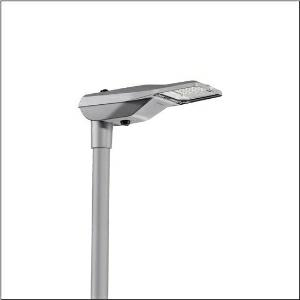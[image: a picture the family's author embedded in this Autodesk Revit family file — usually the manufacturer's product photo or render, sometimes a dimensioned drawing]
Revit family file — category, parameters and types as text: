
# Revit family: streetlight_sl_21_iq_micro___st0_8a_5xe1c31y08db_8273
name_source: partatom
category: Lighting Fixtures
units: mm (PartAtom-declared; Revit-internal decimal feet)

## family parameters
Cut with Voids When Loaded = No
Host = Face
Light Source = No
Part Type = Normal
Room Calculation Point = No
Round Connector Dimension = Use Diameter
Shared = No

## types (1)
- --- (1 x LED, 5110 lm, 39.1 W, 3000K)
    Apparent Load = 39 VA
    CIE Flux Codes = 38 75 97 100 100
    Color Rendering = 70
    Color Temperature = 3000K
    Default Elevation = 1800 mm
    Description = Streetlight SL 21 iQ micro, mast luminaire, primary light control with lens, of PMMA, primary optical cover: cover, of toughened safety glass, transparent, light distribution: ST0.8a, light emission: direct distribution, primary light characteristic: asymmetric, installation type: post-top, side-entry, LED, High Power LED, rated luminous flux: 5.110lm, luminous efficacy: 131lm/W, light colour: 730, colour temperature: 3000K, control gear: iQ-Street Remote, D4i with power reduction, control: pre-setting: logarithmic dimming characteristic, Street-Remote, Auto-Match, Temp-Guard, Lumen-Switch, Night-Set, Smart-Wire, Light-Fading, Desk-Remote (wireless, voltage-free reading and setting of iQ features in the workshop via application-optimized NFC function/RFID function), optimised constant luminous flux control (CLO 2.0), mains connection: 220..240V, AC, 50/60Hz, start of lifetime: 39W, end of service life: 41W, reduction: 17W, luminaire housing, of diecast aluminium, powder-coated, SITECO metallic grey (DB 702S), corrosivity category C5 high according to DIN EN ISO 12944, please order mast flange separately, inclination adjustable: 0°, 5°, 10°, 15°, sealing non-destructively replaceable, multi-level sealing system, length: 528mm, width: 235mm, height: 110mm, mast flange for spigot size: 42mm (side-entry): 5XC10008XM4, 60/48mm (side-entry/post-top): 5XC10108XM2, 76/60mm (side-entry/post-top): 5XC10108XM1, mounting height: 4..8m, Smart Interface below and above, protection rating (complete): IP66, insulation class (complete): insulation class II (safety insulation), certification: CE, ENEC, ENEC+, VDE, impact resistance: IK10, permissible operating ambient temperature for outdoor applications: -40..+50°C, standard-compliant lighting for roads and squares, packaging unit: 1 piece

Light Distribution: ST0.8a
    Height = 110 mm
    Lamp = 1 x LED
    Lamp Light Flux = 5110 lm
    Lamp Power = 39.1 W
    Lamp count = 1
    Length = 528 mm
    Luminous efficacy = 131 lm/W
    Manufacturer = Siteco
    ModVariant = No
    Model = 5XE1C31Y08DB
    Number of Poles = 1
    OnlyDefault = Yes
    Power Factor = 1
    Product Name = Streetlight SL 21 iQ micro | ST0.8a
    Product group = mast luminaire | pylon top
    ProductGroupID = 6100
    Protection Class = Protection class II
    Protection Degree = IP 66
    RLX_Detail_Level = 1
    RLX_Emergency_Light_Flux = 0 lm
    RLX_Emergency_Type = 0
    RLX_Emergency_Type_DB = No
    RlxData = <blob elided: 98705 chars, md5=120f7f2e>
    Socket = socket
    Standby Power = 0 W
    System Light Flux = 5110 lm
    System Power = 39 W
    Type Comments = factory setting: luminous flux: 100 % | dim-lin: 254 | 765 mA
    Type Image = l_1007239.jpg
    URL = http://relux.com
    VarID = @adj_113509
    Voltage = 0 V
    Weight = 0.00 kg
    Width = 235 mm

## geometry (parser evidence)
native form markers: Blend x4, Sweep x9
no freeform markers — native parametric forms only
